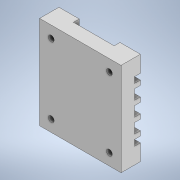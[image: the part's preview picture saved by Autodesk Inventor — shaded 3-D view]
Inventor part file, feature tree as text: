
AUTODESK INVENTOR PART (.ipt)
format: ipt  version: 2020 (Build 240168000, 168)  size: 287,232 bytes
history: native  units: in
note: dims shown in document units (in); Inventor stores cm internally (conversion verified against a paired STEP export)
features: extrude x5, sketch x4, other x3, plane x1, reference x1
ambient origin geometry x8: Origin, YZ Plane, XZ Plane, XY Plane, X Axis, Y Axis, Z Axis, Center Point
bodies: Solid1 (feature_tree)
feature tree (14):
  extrude  "Extrusion1"  Depth=0.21in
  extrude  "Extrusion2"  Depth=0.48in
  plane  "Work Plane1"
  extrude  "Extrusion3"  Depth=0.315in
  extrude  "Extrusion4"  Depth=0.125in TaperAngle=0.0deg
  extrude  "Extrusion5"  TaperAngle=0.0deg  [1 undecoded]
  sketch  "Sketch2"  dims[d0=0.5in d1=0.0in d2=0.21in]
  sketch  "Sketch3"  dims[d3=3.0in d4=0.0in d6=0.48in]
  reference  "Reference4"
  sketch  "Sketch4"  dims[d7=0.1in d8=1.5748in d10=0.315in d11=0.3937in d13=1.0in]
  sketch  "Sketch5"  dims[d15=0.21in d16=0.0in d19=0.21in d20=0.0in d21=0.0in d22=0.085in d23=0.0in d26=2.0in d27=1.75in d28=0.25in d29=0.25in d30=0.25in d31=0.25in d32=0.25in d33=0.25in d34=0.25in d35=0.25in d40=0.125in d41=0.125in d42=0.125in d43=0.125in d44=0.125in d45=0.125in d46=0.125in d47=0.125in d5=0.0344in]
  other  "<userpath>\Desktop\PnP Machine\PnP Machine.iam"
  other  "PnP Machine.iam"
  other  "Transmission Clamp:2"
note: 1 required parameter value undecoded (feature->parameter linkage not recoverable at this tier; creation-order binding heuristic only, values carry confidence <= 0.55)
